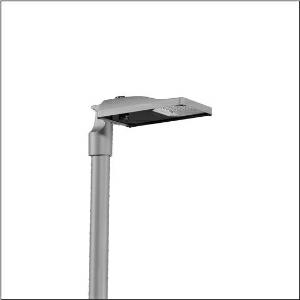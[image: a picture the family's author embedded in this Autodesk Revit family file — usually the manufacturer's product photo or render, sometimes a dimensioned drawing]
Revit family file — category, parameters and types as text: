
# Revit family: streetlight_sl_31_micro___pl52_5xh5h31t08da_3d46
name_source: partatom
category: Lighting Fixtures
units: mm (PartAtom-declared; Revit-internal decimal feet)

## family parameters
Cut with Voids When Loaded = No
Host = Face
Light Source = No
Part Type = Normal
Room Calculation Point = No
Round Connector Dimension = Use Diameter
Shared = No

## types (1)
- --- (1 x LED, 4850 lm, 37.7 W, 3000K)
    Apparent Load = 38 VA
    CIE Flux Codes = 27 59 98 100 100
    Color Rendering = 70
    Color Temperature = 3000K
    Default Elevation = 1800 mm
    Description = Streetlight SL 31 micro D4i, Desk-Remote mast luminaire for post-top, side-entry; light control with lens of PMMA; light distribution: PL52, direct asymmetric distribution, for standard-compliant lighting for roads and squares; LED: luminous flux: 4.850lm, light colour: 730, colour temperature: 3000K; luminous efficacy: 128,6lm/W; control: pre-setting: logarithmic dimming characteristic, flexible luminous flux parameterisation, time-dependent luminous flux control, constant luminous flux control, power reduction, intelligent temperature release in ECG and LED module, overheat protection; luminaire housing, of diecast aluminium, Siteco® metallic grey (DB 702S), corrosivity category C5 high according to DIN EN ISO 12944; cover of toughened safety glass, transparent, opened without tools; mast flange of diecast aluminium, Siteco® metallic grey (DB 702S), spigot size: 76/60mm, mast flange included unmounted; with cable H07RN-F 2x 1.5mm², cable length: 6,5m, connection cable pre-assembled; mains connection: 220..240V, AC, 50/60Hz; power consumption (at start of service life): 37,7W / (at end of service life): 40,9W / (with reduced operation 50%): 16,3W; protection rating (complete): IP66; insulation class (complete): insulation class II (safety insulation); impact resistance: IK09; certification: CE, ENEC, ENEC+, VDE, UKCA, ZD4i; permissible operating ambient temperature for outdoor applications: -40..+50°C; packaging unit: 1 piece

Light Distribution: PL52
    Height = 76 mm
    Lamp = 1 x LED
    Lamp Light Flux = 4850 lm
    Lamp Power = 37.7 W
    Lamp count = 1
    Length = 467 mm
    Luminous efficacy = 129 lm/W
    Manufacturer = Siteco
    ModVariant = No
    Model = 5XH5H31T08DA
    Number of Poles = 1
    OnlyDefault = Yes
    Power Factor = 1
    Product Name = Streetlight SL 31 micro | PL52
    Product group = mast luminaire | pylon top
    ProductGroupID = 6100
    Protection Class = Protection class II
    Protection Degree = IP 66
    RLX_Detail_Level = 1
    RLX_Emergency_Light_Flux = 0 lm
    RLX_Emergency_Type = 0
    RLX_Emergency_Type_DB = No
    RlxData = <blob elided: 53749 chars, md5=a743db57>
    Socket = socket
    Standby Power = 0 W
    System Light Flux = 4850 lm
    System Power = 38 W
    Type Comments = factory setting: luminous flux: 100 % | dim-lin: 254 | 745 mA
    Type Image = l_1300315.jpg
    URL = http://relux.com
    VarID = @adj_048302
    Voltage = 0 V
    Weight = 0.00 kg
    Width = 265 mm

## geometry (parser evidence)
native form markers: Blend x4, Sweep x13
no freeform markers — native parametric forms only
